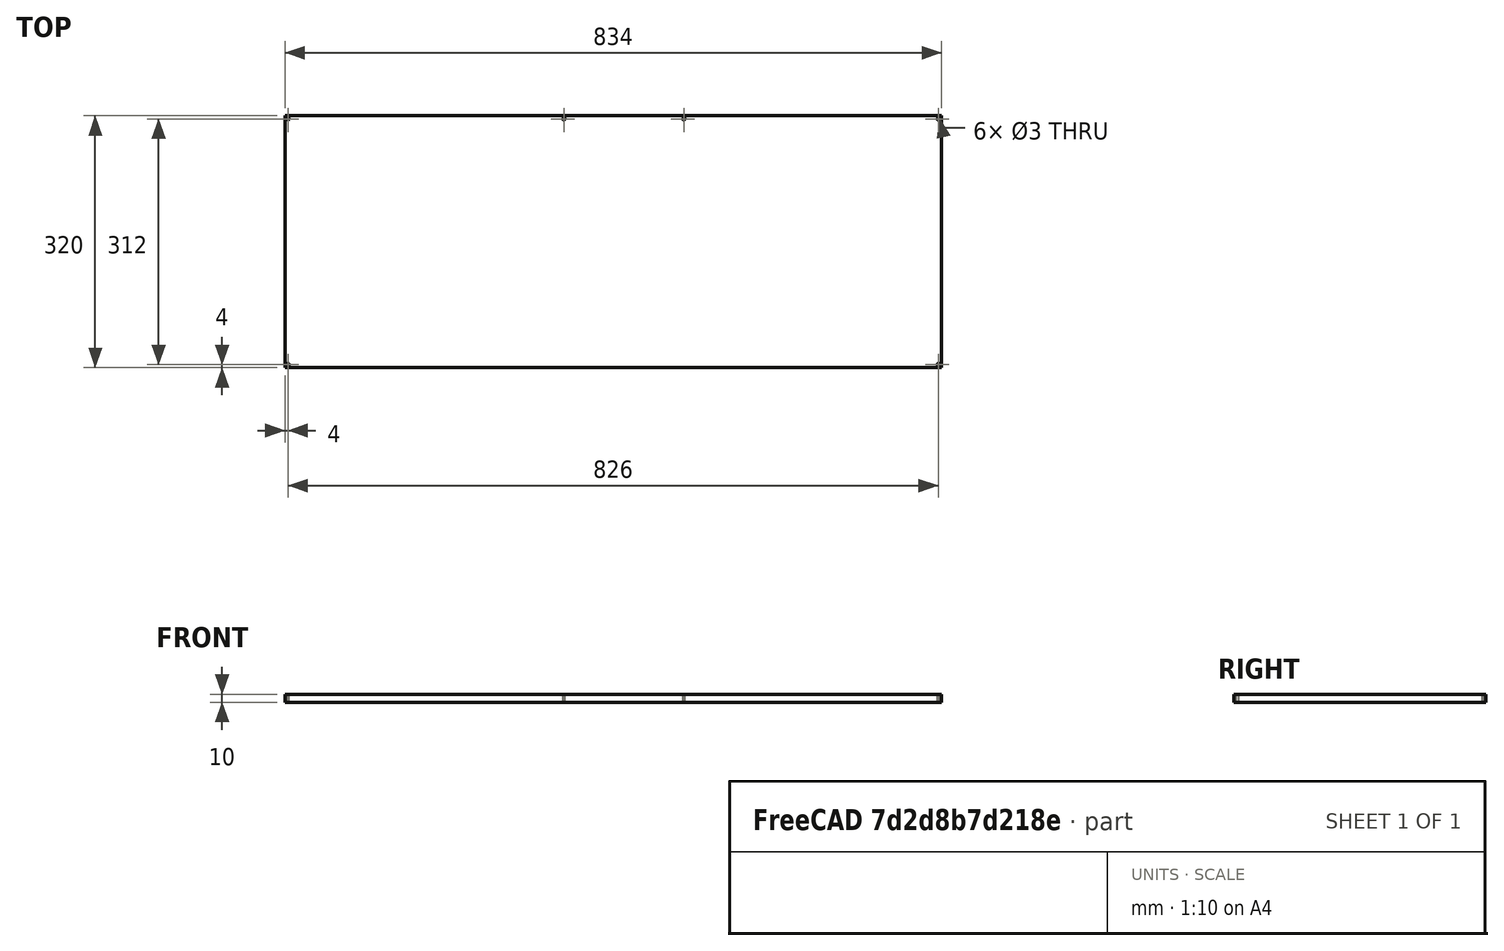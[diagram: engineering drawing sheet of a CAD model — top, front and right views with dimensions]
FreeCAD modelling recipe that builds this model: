
FCSTD DOCUMENT  (FreeCAD 0.21R33771 (Git))
Label: panel2_devkit_mount
License: All rights reserved
LicenseURL: https://en.wikipedia.org/wiki/All_rights_reserved
objects: Sketcher::SketchObject×4, PartDesign::Pad×1, PartDesign::Body×1
note: 7 computed .brp shape members not serialized (recipe doc carries the construction recipe); baked Part::Feature solids carry a one-line shape summary decoded from their .brp

FEATURE [Sketcher::SketchObject] Sketch
  FullyConstrained = false
  MapMode = 5
  Support = -> [XY_Plane]
  sketch-geometry (10):
    g0: LineSegment StartX=-417 StartY=160 StartZ=0 EndX=417 EndY=160 EndZ=0
    g1: LineSegment StartX=417 StartY=160 StartZ=0 EndX=417 EndY=-160 EndZ=0
    g2: LineSegment StartX=417 StartY=-160 StartZ=0 EndX=-417 EndY=-160 EndZ=0
    g3: LineSegment StartX=-417 StartY=-160 StartZ=0 EndX=-417 EndY=160 EndZ=0
    g4: Circle CenterX=-413 CenterY=-156 CenterZ=0 NormalX=0 NormalY=0 NormalZ=1 AngleXU=0 Radius=1.5
    g5: Circle CenterX=-413 CenterY=156 CenterZ=0 NormalX=0 NormalY=0 NormalZ=1 AngleXU=0 Radius=1.5
    g6: Circle CenterX=413 CenterY=-156 CenterZ=0 NormalX=0 NormalY=0 NormalZ=1 AngleXU=0 Radius=1.5
    g7: Circle CenterX=413 CenterY=156 CenterZ=0 NormalX=0 NormalY=0 NormalZ=1 AngleXU=0 Radius=1.5
    g8: Circle CenterX=-62.6117 CenterY=156 CenterZ=0 NormalX=0 NormalY=0 NormalZ=1 AngleXU=0 Radius=1.5
    g9: Circle CenterX=89.7883 CenterY=156 CenterZ=0 NormalX=0 NormalY=0 NormalZ=1 AngleXU=0 Radius=1.5
  constraints (24):
    c: Coincident(g0,g1)
    c: Coincident(g1,g2)
    c: Coincident(g2,g3)
    c: Coincident(g3,g0)
    c: Horizontal(g0)
    c: Horizontal(g2)
    c: Vertical(g1)
    c: Vertical(g3)
    c: DistanceY(g3,g3) = 320
    c: DistanceX(g0,g0) = 834
    c: Diameter(g4) = 3
    c: Distance(g4,g2) = 4
    c: Distance(g4,g3) = 4
    c: Symmetric(g0,g2,g-1)
    c: Diameter(g5) = 3
    c: Distance(g5,g0) = 4
    c: Distance(g5,g3) = 4
    c: Diameter(g6) = 3
    c: Diameter(g7) = 3
    c: Diameter(g8) = 3
    c: Horizontal(g5,g8)
    c: Diameter(g9) = 3
    c: Horizontal(g8,g9)
    c: DistanceX(g8,g9) = 152.4
FEATURE [PartDesign::Pad] Pad
  Direction = (0,0,1)
  Length = 10
  Length2 = 10
  Profile = -> Sketch
  ReferenceAxis = -> Sketch [N_Axis]
  Type = 0
FEATURE [PartDesign::Body] Body
  Group = -> [Sketch,Pad]
  Origin = -> Origin
  Tip = -> Pad
FEATURE [Sketcher::SketchObject] Sketch003  label="ads9-v2ebz"
  FullyConstrained = false
  MapMode = 5
  Placement = pos=(0,0,10) rot=(0,0,1;0rad)
  Support = -> [Pad]
  sketch-geometry (20):
    g0: LineSegment StartX=1000.15 StartY=-52.0543 StartZ=0 EndX=740.442 EndY=-52.0543 EndZ=0
    g1: LineSegment StartX=740.442 StartY=-52.0543 StartZ=0 EndX=740.432 EndY=163.846 EndZ=0
    g2: LineSegment StartX=740.432 StartY=163.846 StartZ=0 EndX=1000.14 EndY=163.846 EndZ=0
    g3: LineSegment StartX=1000.14 StartY=163.846 StartZ=0 EndX=1000.15 EndY=-52.0543 EndZ=0
    g4: Circle CenterX=962.632 CenterY=127.531 CenterZ=0 NormalX=0 NormalY=0 NormalZ=1 AngleXU=0 Radius=1.5
    g5: Circle CenterX=842.162 CenterY=145.438 CenterZ=0 NormalX=0 NormalY=0 NormalZ=1 AngleXU=0 Radius=1.5
    g6: Circle CenterX=850.872 CenterY=48.8929 CenterZ=0 NormalX=0 NormalY=0 NormalZ=1 AngleXU=0 Radius=1.5
    g7: Circle CenterX=962.632 CenterY=30.5033 CenterZ=0 NormalX=0 NormalY=0 NormalZ=1 AngleXU=0 Radius=1.5
    g8: Circle CenterX=986.462 CenterY=136.066 CenterZ=0 NormalX=0 NormalY=0 NormalZ=1 AngleXU=0 Radius=1.5
    g9: Circle CenterX=746.912 CenterY=-43.8298 CenterZ=0 NormalX=0 NormalY=0 NormalZ=1 AngleXU=0 Radius=1.5
    g10: Circle CenterX=746.912 CenterY=156.83 CenterZ=0 NormalX=0 NormalY=0 NormalZ=1 AngleXU=0 Radius=1.5
    g11: Circle CenterX=896.772 CenterY=21.2577 CenterZ=0 NormalX=0 NormalY=0 NormalZ=1 AngleXU=0 Radius=1.5
    g12: Circle CenterX=991.382 CenterY=156.83 CenterZ=0 NormalX=0 NormalY=0 NormalZ=1 AngleXU=0 Radius=1.5
    g13: Circle CenterX=988.842 CenterY=43.8002 CenterZ=0 NormalX=0 NormalY=0 NormalZ=1 AngleXU=0 Radius=1.5
    g14: Circle CenterX=991.382 CenterY=-43.8298 CenterZ=0 NormalX=0 NormalY=0 NormalZ=1 AngleXU=0 Radius=1.5
    g15: Circle CenterX=986.302 CenterY=53.2617 CenterZ=0 NormalX=0 NormalY=0 NormalZ=1 AngleXU=0 Radius=1.5
    g16: Circle CenterX=982.112 CenterY=-42.8773 CenterZ=0 NormalX=0 NormalY=0 NormalZ=1 AngleXU=0 Radius=1.5
    g17: Circle CenterX=889.152 CenterY=21.2577 CenterZ=0 NormalX=0 NormalY=0 NormalZ=1 AngleXU=0 Radius=1.5
    g18: Circle CenterX=754.152 CenterY=155.51 CenterZ=0 NormalX=0 NormalY=0 NormalZ=1 AngleXU=0 Radius=1.5
    g19: Circle CenterX=748.182 CenterY=-36.6543 CenterZ=0 NormalX=0 NormalY=0 NormalZ=1 AngleXU=0 Radius=1.5
  constraints (25):
    c: Coincident(g0,g1)
    c: Coincident(g1,g2)
    c: Coincident(g2,g3)
    c: Coincident(g3,g0)
    c: Parallel(g1,g3)
    c: Parallel(g2,g0)
    c: DistanceY(g1,g1) = 215.9
    c: DistanceX(g2,g2) = 259.71
    c: DistanceX(g1,g10) = 6.48
    c: DistanceX(g10,g18) = 7.24
    c: DistanceY(g18,g10) = 1.32
    c: DistanceX(g0,g19) = 7.74
    c: DistanceX(g0,g9) = 6.47
    c: DistanceX(g0,g6) = 110.43
    c: DistanceX(g17,g0) = 111
    c: DistanceX(g11,g0) = 103.38
    c: DistanceX(g16,g0) = 18.04
    c: DistanceX(g14,g0) = 8.77
    c: DistanceX(g7,g0) = 37.52
    c: DistanceX(g13,g2) = 11.3
    c: DistanceX(g15,g2) = 13.84
    c: DistanceX(g4,g2) = 37.51
    c: DistanceX(g8,g2) = 13.68
    c: DistanceX(g12,g2) = 8.76
    c: DistanceX(g1,g5) = 101.73
FEATURE [Sketcher::SketchObject] Sketch004  label="eval-adrv9026"
  FullyConstrained = false
  MapMode = 5
  Placement = pos=(0,0,10) rot=(0,0,1;0rad)
  Support = -> [Pad]
  sketch-geometry (14):
    g0: LineSegment StartX=-75.2784 StartY=53.8564 StartZ=0 EndX=142.654 EndY=53.8564 EndZ=0
    g1: LineSegment StartX=142.654 StartY=53.8564 StartZ=0 EndX=142.654 EndY=-139.184 EndZ=0
    g2: LineSegment StartX=142.654 StartY=-139.184 StartZ=0 EndX=-75.2784 EndY=-139.184 EndZ=0
    g3: LineSegment StartX=-75.2784 StartY=-139.184 StartZ=0 EndX=-75.2784 EndY=-77.7156 EndZ=0
    g4: LineSegment StartX=-94.0744 StartY=-7.3576 StartZ=0 EndX=-75.2784 EndY=-7.3576 EndZ=0
    g5: LineSegment StartX=-75.2784 StartY=-77.7156 StartZ=0 EndX=-94.0744 EndY=-77.7156 EndZ=0
    g6: LineSegment StartX=-94.0744 StartY=-77.7156 StartZ=0 EndX=-94.0744 EndY=-7.3576 EndZ=0
    g7: LineSegment StartX=-75.2784 StartY=-7.3576 StartZ=0 EndX=-75.2784 EndY=53.8564 EndZ=0
    g8: Circle CenterX=126.112 CenterY=25.9164 CenterZ=0 NormalX=0 NormalY=0 NormalZ=1 AngleXU=0 Radius=1.5
    g9: Circle CenterX=126.112 CenterY=-111.244 CenterZ=0 NormalX=0 NormalY=0 NormalZ=1 AngleXU=0 Radius=1.5
    g10: GeomPoint X=142.654 Y=-42.6636 Z=0
    g11: Circle CenterX=19.4319 CenterY=38.6164 CenterZ=0 NormalX=0 NormalY=0 NormalZ=1 AngleXU=0 Radius=1.5
    g12: Circle CenterX=19.4319 CenterY=-123.944 CenterZ=0 NormalX=0 NormalY=0 NormalZ=1 AngleXU=0 Radius=1.5
    g13: GeomPoint X=57.5319 Y=-42.6636 Z=0
  constraints (38):
    c: Coincident(g0,g1)
    c: Coincident(g1,g2)
    c: Coincident(g2,g3)
    c: Coincident(g7,g0)
    c: Horizontal(g0)
    c: Horizontal(g2)
    c: Vertical(g1)
    c: Vertical(g3)
    c: Coincident(g5,g6)
    c: Coincident(g6,g4)
    c: Horizontal(g4)
    c: Horizontal(g5)
    c: Vertical(g6)
    c: DistanceY(g1,g1) = 193.04
    c: DistanceX(g0,g0) = 217.932
    c: Coincident(g5,g3)
    c: Coincident(g4,g7)
    c: DistanceY(g3,g3) = 61.468
    c: Parallel(g7,g1)
    c: DistanceX(g4,g4) = 18.796
    c: Equal(g2,g0)
    c: Diameter(g8) = 3
    c: Diameter(g9) = 3
    c: DistanceY(g9,g8) = 137.16
    c: DistanceY(g6,g6) = 70.358
    c: PointOnObject(g10,g1)
    c: Distance(g0,g10) = 96.52
    c: DistanceY(g10,g8) = 68.58
    c: Vertical(g8,g9)
    c: Diameter(g11) = 3
    c: DistanceY(g10,g11) = 81.28
    c: Diameter(g12) = 3
    c: Vertical(g11,g12)
    c: DistanceY(g12,g10) = 81.28
    c: DistanceX(g11,g8) = 106.68
    c: DistanceY(g13,g0) = 96.52
    c: DistanceX(g4,g13) = 151.606
    c: DistanceX(g13,g9) = 68.58
FEATURE [Sketcher::SketchObject] Sketch005
  FullyConstrained = false
  MapMode = 2
  sketch-geometry (31):
    g0: LineSegment StartX=-437 StartY=180 StartZ=0 EndX=437 EndY=180 EndZ=0
    g1: LineSegment StartX=437 StartY=180 StartZ=0 EndX=437 EndY=-180 EndZ=0
    g2: LineSegment StartX=437 StartY=-180 StartZ=0 EndX=-437 EndY=-180 EndZ=0
    g3: LineSegment StartX=-437 StartY=-180 StartZ=0 EndX=-437 EndY=180 EndZ=0
    g4: Circle CenterX=-413 CenterY=-1.02831e-05 CenterZ=0 NormalX=0 NormalY=0 NormalZ=1 AngleXU=0 Radius=1.5
    g5: Circle CenterX=-413 CenterY=-156 CenterZ=0 NormalX=0 NormalY=0 NormalZ=1 AngleXU=0 Radius=1.5
    g6: Circle CenterX=-335 CenterY=31.75 CenterZ=0 NormalX=0 NormalY=0 NormalZ=1 AngleXU=0 Radius=3.175
    g7: Circle CenterX=-257 CenterY=156 CenterZ=0 NormalX=0 NormalY=0 NormalZ=1 AngleXU=0 Radius=1.4986
    g8: Circle CenterX=-335 CenterY=-31.75 CenterZ=0 NormalX=0 NormalY=0 NormalZ=1 AngleXU=0 Radius=3.175
    g9: Circle CenterX=-257 CenterY=0 CenterZ=0 NormalX=0 NormalY=0 NormalZ=1 AngleXU=0 Radius=1.5
    g10: Circle CenterX=-255 CenterY=-156 CenterZ=0 NormalX=0 NormalY=0 NormalZ=1 AngleXU=0 Radius=1.5
    g11: Circle CenterX=-101 CenterY=156 CenterZ=0 NormalX=0 NormalY=0 NormalZ=1 AngleXU=0 Radius=1.5
    g12: Circle CenterX=-101 CenterY=0 CenterZ=0 NormalX=0 NormalY=0 NormalZ=1 AngleXU=0 Radius=1.5
    g13: Circle CenterX=-97 CenterY=-156 CenterZ=0 NormalX=0 NormalY=0 NormalZ=1 AngleXU=0 Radius=1.5
    g14: LineSegment StartX=0 StartY=180 StartZ=0 EndX=0 EndY=-180 EndZ=0
    g15: Circle CenterX=413 CenterY=156 CenterZ=0 NormalX=0 NormalY=0 NormalZ=1 AngleXU=0 Radius=1.5
    g16: Circle CenterX=413 CenterY=-1.21668e-11 CenterZ=0 NormalX=0 NormalY=0 NormalZ=1 AngleXU=0 Radius=1.5
    g17: Circle CenterX=413 CenterY=-156 CenterZ=0 NormalX=0 NormalY=0 NormalZ=1 AngleXU=0 Radius=1.5
    g18: Circle CenterX=335 CenterY=31.75 CenterZ=0 NormalX=0 NormalY=0 NormalZ=1 AngleXU=0 Radius=3.175
    g19: Circle CenterX=257 CenterY=156 CenterZ=0 NormalX=0 NormalY=0 NormalZ=1 AngleXU=0 Radius=1.5
    g20: Circle CenterX=335 CenterY=-31.75 CenterZ=0 NormalX=0 NormalY=0 NormalZ=1 AngleXU=0 Radius=3.175
    g21: Circle CenterX=257 CenterY=0 CenterZ=0 NormalX=0 NormalY=0 NormalZ=1 AngleXU=0 Radius=1.5
    g22: Circle CenterX=255 CenterY=-156 CenterZ=0 NormalX=0 NormalY=0 NormalZ=1 AngleXU=0 Radius=1.5
    g23: Circle CenterX=101 CenterY=156 CenterZ=0 NormalX=0 NormalY=0 NormalZ=1 AngleXU=0 Radius=1.5
    g24: Circle CenterX=101 CenterY=0 CenterZ=0 NormalX=0 NormalY=0 NormalZ=1 AngleXU=0 Radius=1.5
    g25: Circle CenterX=97 CenterY=-156 CenterZ=0 NormalX=0 NormalY=0 NormalZ=1 AngleXU=0 Radius=1.5
    g26: Circle CenterX=-31.75 CenterY=31.75 CenterZ=0 NormalX=0 NormalY=0 NormalZ=1 AngleXU=0 Radius=3.175
    g27: Circle CenterX=-31.75 CenterY=-31.75 CenterZ=0 NormalX=0 NormalY=0 NormalZ=1 AngleXU=0 Radius=3.175
    g28: Circle CenterX=31.75 CenterY=31.75 CenterZ=0 NormalX=0 NormalY=0 NormalZ=1 AngleXU=0 Radius=3.175
    g29: Circle CenterX=31.75 CenterY=-31.75 CenterZ=0 NormalX=0 NormalY=0 NormalZ=1 AngleXU=0 Radius=3.175
    g30: Circle CenterX=-413 CenterY=156 CenterZ=0 NormalX=0 NormalY=0 NormalZ=1 AngleXU=0 Radius=1.4986
  constraints (65):
    c: Coincident(g0,g1)
    c: Coincident(g1,g2)
    c: Coincident(g2,g3)
    c: Coincident(g3,g0)
    c: Horizontal(g0)
    c: Horizontal(g2)
    c: Vertical(g1)
    c: DistanceX(g0,g0) = 874
    c: DistanceY(g1,g1) = 360
    c: Diameter(g4) = 3
    c: Diameter(g5) = 3
    c: Diameter(g6) = 6.35
    c: Diameter(g7) = 2.9972
    c: Diameter(g8) = 6.35
    c: Distance(g4,g3) = 24
    c: Distance(g5,g3) = 24
    c: Diameter(g9) = 3
    c: Diameter(g10) = 3
    c: Distance(g4,g5) = 156
    c: DistanceX(g4,g8) = 78
    c: DistanceX(g6,g9) = 78
    c: Distance(g7,g0) = 24
    c: DistanceX(g5,g10) = 158
    c: Distance(g10,g2) = 24
    c: Diameter(g11) = 3
    c: Diameter(g12) = 3
    c: Diameter(g13) = 3
    c: DistanceX(g7,g11) = 156
    c: Distance(g11,g0) = 24
    c: DistanceX(g4,g6) = 78
    c: DistanceX(g9,g12) = 156
    c: DistanceX(g10,g13) = 158
    c: Distance(g13,g2) = 24
    c: PointOnObject(g14,g0)
    c: PointOnObject(g14,g2)
    c: Vertical(g14)
    c: DistanceX(g14,g0) = 437
    c: Symmetric(g0,g2,g-1)
    c: Distance(g6,g-1) = 31.75
    c: Distance(g8,g-1) = 31.75
    c: PointOnObject(g9,g-1)
    c: PointOnObject(g12,g-1)
    c: PointOnObject(g-1,g14)
    c: Diameter(g15) = 3
    c: Diameter(g16) = 3
    c: Diameter(g17) = 3
    c: Diameter(g18) = 6.35
    c: Diameter(g19) = 3
    c: Diameter(g20) = 6.35
    c: Distance(g15,g16) = 156
    c: Diameter(g21) = 3
    c: Diameter(g22) = 3
    c: Distance(g16,g17) = 156
    c: Diameter(g23) = 3
    c: Diameter(g24) = 3
    c: Diameter(g25) = 3
    c: Diameter(g26) = 6.35
    c: Distance(g26,g-1) = 31.75
    c: Distance(g26,g14) = 31.75
    c: Diameter(g27) = 6.35
    c: Diameter(g28) = 6.35
    c: Diameter(g29) = 6.35
    c: Diameter(g30) = 2.9972
    c: Distance(g30,g3) = 24
    c: Distance(g30,g0) = 24
